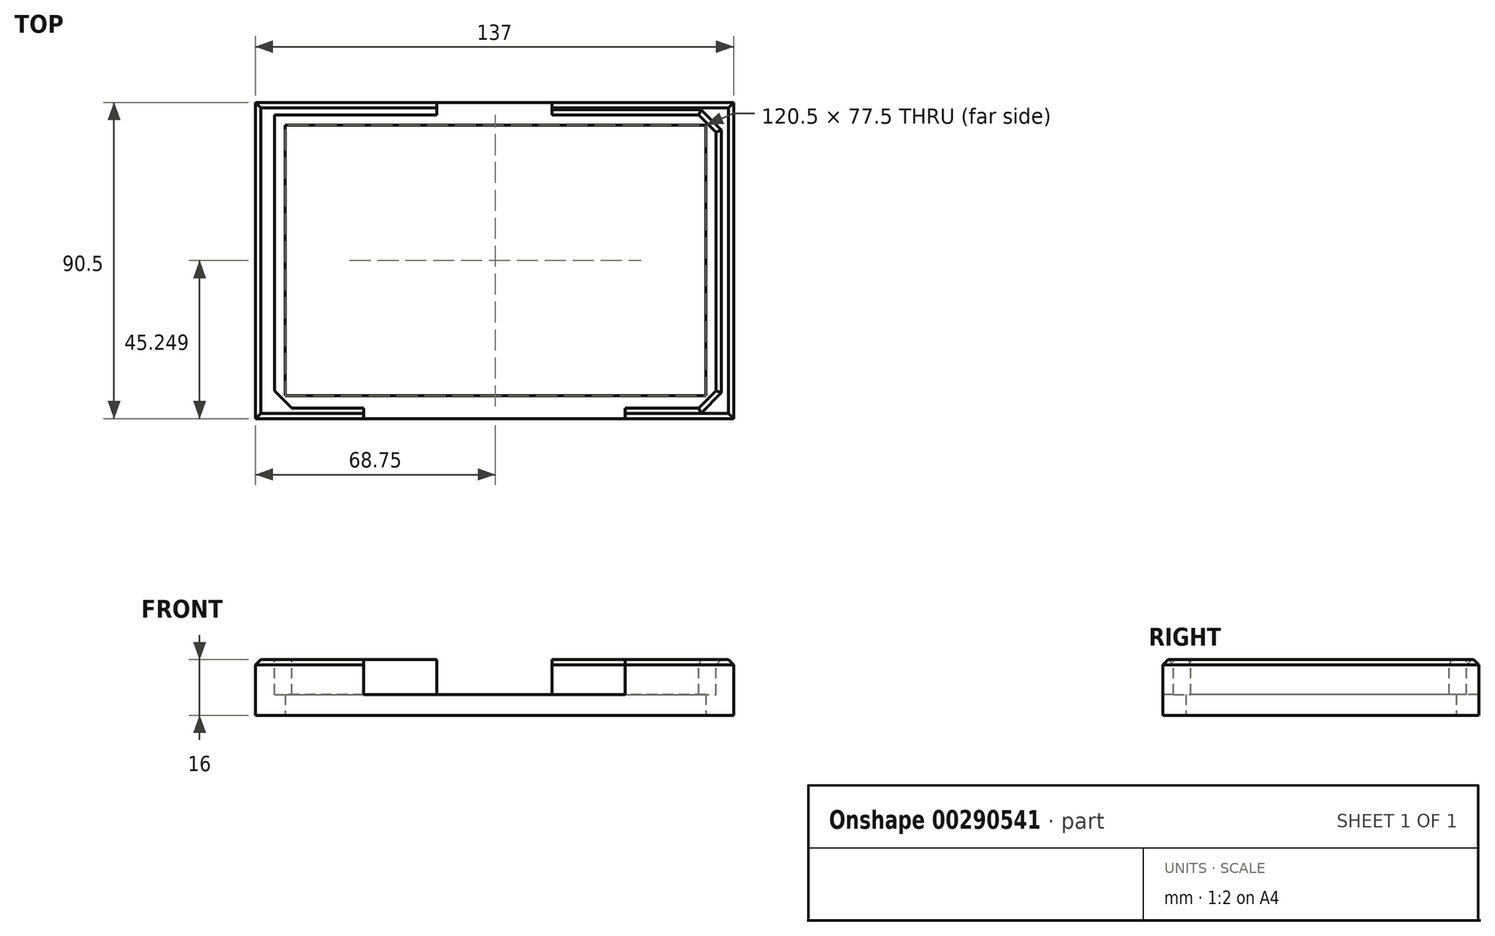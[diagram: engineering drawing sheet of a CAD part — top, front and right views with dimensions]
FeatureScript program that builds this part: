
annotation { "Feature Type Name" : "Feature", "Feature Type Description" : "" }
export const myFeature = defineFeature(function(context is Context, id is Id, definition is map)
    precondition{}
    {
        {
            var Q0;
            Q0=qCreatedBy(makeId("Top.planeOp"),FACE);
            var sketch = newSketch(context, id + "F0", { "sketchPlane" : qUnion([Q0])});
            skLineSegment(sketch, "E0.top", {"start": v(-58.19, -26.41) * mm, "end": v(78.81, -26.41) * mm});
            skLineSegment(sketch, "E0.left", {"start": v(-58.19, 64.09) * mm, "end": v(-58.19, -26.41) * mm});
            skLineSegment(sketch, "E0.right", {"start": v(78.81, 64.09) * mm, "end": v(78.81, -26.41) * mm});
            skLineSegment(sketch, "E1.top", {"start": v(-49.69, -19.91) * mm, "end": v(70.81, -19.91) * mm});
            skLineSegment(sketch, "E1.left", {"start": v(-49.69, 57.59) * mm, "end": v(-49.69, -19.91) * mm});
            skLineSegment(sketch, "E1.right", {"start": v(70.81, 57.59) * mm, "end": v(70.81, -19.91) * mm});
            skLineSegment(sketch, "E2", {"start": v(-58.19, 64.09) * mm, "end": v(78.81, 64.09) * mm});
            skLineSegment(sketch, "E3", {"start": v(70.81, 57.59) * mm, "end": v(-49.69, 57.59) * mm});
            skSolve(sketch);
        }
        {
            var Q0;
            Q0=makeQuery(id+"F0.imprint","IMPRINT",FACE,{"disambiguationData":[TD([[makeQuery(id+"F0.imprint","IMPRINT",EDGE,{"derivedFrom":sQuery(id+"F0.wireOp",EDGE,"E0.top")}),1.0]])]});
            extrude(context, id + "F1", {"entities" : qUnion([Q0]), "depth" : 16 * mm});
        }
        {
            var Q0;
            Q0=makeQuery(id+"F1.opExtrude","CAP_VERTEX",VERTEX,{"disambiguationData":[OSD([sQuery(id+"F0.wireOp",EDGE,"E0.left"),sQuery(id+"F0.wireOp",EDGE,"E2")])],"isStart":false});
            var Q1;
            Q1=makeQuery(id+"F1.opExtrude","CAP_VERTEX",VERTEX,{"disambiguationData":[OSD([sQuery(id+"F0.wireOp",EDGE,"E1.left"),sQuery(id+"F0.wireOp",EDGE,"E3")])],"isStart":false});
            var Q2;
            Q2=makeQuery(id+"F1.opExtrude","CAP_VERTEX",VERTEX,{"disambiguationData":[OSD([sQuery(id+"F0.wireOp",EDGE,"E1.top"),sQuery(id+"F0.wireOp",EDGE,"E1.left")])],"isStart":false});
            cPlane(context, id + "F2", {"entities" : qUnion([Q0, Q1, Q2]), "cplaneType" : CPlaneType.THREE_POINT, "offset" : 25 * mm, "width" : 150 * mm, "height" : 150 * mm});
        }
        {
            var Q0;
            Q0=qCreatedBy(id+"F2.planeOp",FACE);
            var sketch = newSketch(context, id + "F3", { "sketchPlane" : qUnion([Q0])});
            skLineSegment(sketch, "E4.bottom", {"start": v(-6.19, 80.88) * mm, "end": v(26.81, 80.88) * mm});
            skLineSegment(sketch, "E4.top", {"start": v(-6.19, 32.2) * mm, "end": v(26.81, 32.2) * mm});
            skLineSegment(sketch, "E4.left", {"start": v(-6.19, 80.88) * mm, "end": v(-6.19, 32.2) * mm});
            skLineSegment(sketch, "E4.right", {"start": v(26.81, 80.88) * mm, "end": v(26.81, 32.2) * mm});
            skLineSegment(sketch, "E5.bottom", {"start": v(-52.69, 60.59) * mm, "end": v(68.81, 60.59) * mm});
            skLineSegment(sketch, "E5.top", {"start": v(-47.69, -23.41) * mm, "end": v(68.81, -23.41) * mm});
            skLineSegment(sketch, "E5.left", {"start": v(-52.69, 60.59) * mm, "end": v(-52.69, -18.41) * mm});
            skLineSegment(sketch, "E6.bottom", {"start": v(47.81, -13.81) * mm, "end": v(-27.19, -13.81) * mm});
            skLineSegment(sketch, "E6.top", {"start": v(47.81, -33.81) * mm, "end": v(-27.19, -33.81) * mm});
            skLineSegment(sketch, "E6.left", {"start": v(47.81, -13.81) * mm, "end": v(47.81, -33.81) * mm});
            skLineSegment(sketch, "E6.right", {"start": v(-27.19, -13.81) * mm, "end": v(-27.19, -33.81) * mm});
            skLineSegment(sketch, "E7", {"start": v(-52.69, -18.41) * mm, "end": v(-47.69, -23.41) * mm});
            skLineSegment(sketch, "E8", {"start": v(68.81, -23.41) * mm, "end": v(73.81, -18.41) * mm});
            skLineSegment(sketch, "E9", {"start": v(68.81, 60.59) * mm, "end": v(73.81, 55.59) * mm});
            skLineSegment(sketch, "E10", {"start": v(73.81, 55.59) * mm, "end": v(73.81, -18.41) * mm});
            skSolve(sketch);
        }
        {
            var Q0;
            {var subQ0=sQuery(id+"F3.wireOp",EDGE,"E4.bottom");Q0=makeQuery(id+"F3.imprint","IMPRINT",FACE,{"disambiguationData":[TD([[makeQuery(id+"F3.imprint","IMPRINT",EDGE,{"derivedFrom":subQ0}),-1.0]])]});}
            var Q1;
            {var subQ0=sQuery(id+"F3.wireOp",EDGE,"E4.top");Q1=makeQuery(id+"F3.imprint","IMPRINT",FACE,{"disambiguationData":[TD([[makeQuery(id+"F3.imprint","IMPRINT",EDGE,{"derivedFrom":subQ0}),1.0]])]});}
            var Q2;
            {var subQ10=sQuery(id+"F3.wireOp",EDGE,"E4.top");Q2=makeQuery(id+"F3.imprint","IMPRINT",FACE,{"disambiguationData":[TD([[makeQuery(id+"F3.imprint","IMPRINT",EDGE,{"derivedFrom":subQ10}),-1.0]])]});}
            var Q3;
            {var subQ5=sQuery(id+"F3.wireOp",EDGE,"E6.bottom");Q3=makeQuery(id+"F3.imprint","IMPRINT",FACE,{"disambiguationData":[TD([[makeQuery(id+"F3.imprint","IMPRINT",EDGE,{"derivedFrom":subQ5}),1.0]])]});}
            var Q4;
            {var subQ5=sQuery(id+"F3.wireOp",EDGE,"E6.top");Q4=makeQuery(id+"F3.imprint","IMPRINT",FACE,{"disambiguationData":[TD([[makeQuery(id+"F3.imprint","IMPRINT",EDGE,{"derivedFrom":subQ5}),-1.0]])]});}
            extrude(context, id + "F4", {"entities" : qUnion([Q0, Q1, Q2, Q3, Q4]), "operationType" : NewBodyOperationType.REMOVE, "oppositeDirection" : true, "depth" : 10 * mm});
        }
        {
            var Q0;
            Q0=makeQuery(id+"F4.boolean.opBoolean","COPY",EDGE,{"derivedFrom":makeQuery(id+"F4.opExtrude","CAP_EDGE",EDGE,{"disambiguationData":[OSD([sQuery(id+"F3.wireOp",EDGE,"E5.left")])],"isStart":true})});
            var Q1;
            {var subQ0=sQuery(id+"F3.wireOp",EDGE,"E5.bottom");Q1=makeQuery(id+"F4.boolean.opBoolean","COPY",EDGE,{"derivedFrom":makeQuery(id+"F4.opExtrude","CAP_EDGE",EDGE,{"disambiguationData":[OSD([subQ0]),TDD([makeQuery(id+"F3.imprint","IMPRINT",EDGE,{"disambiguationData":[TD([[makeQuery(id+"F3.imprint","INTERSECT",VERTEX,{"derivedFrom":[subQ0,sQuery(id+"F3.wireOp",EDGE,"E5.left")]}),-1.0]])],"derivedFrom":subQ0})])],"isStart":true})});}
            var Q2;
            {var subQ0=sQuery(id+"F3.wireOp",EDGE,"E5.bottom");Q2=makeQuery(id+"F4.boolean.opBoolean","COPY",EDGE,{"derivedFrom":makeQuery(id+"F4.opExtrude","CAP_EDGE",EDGE,{"disambiguationData":[OSD([subQ0]),TDD([makeQuery(id+"F3.imprint","IMPRINT",EDGE,{"disambiguationData":[TD([[makeQuery(id+"F3.imprint","INTERSECT",VERTEX,{"derivedFrom":[subQ0,sQuery(id+"F3.wireOp",EDGE,"E5.right")]}),1.0]])],"derivedFrom":subQ0})])],"isStart":true})});}
            var Q3;
            Q3=makeQuery(id+"F4.boolean.opBoolean","COPY",EDGE,{"derivedFrom":makeQuery(id+"F4.opExtrude","CAP_EDGE",EDGE,{"disambiguationData":[OSD([sQuery(id+"F3.wireOp",EDGE,"E5.right")])],"isStart":true})});
            var Q4;
            {var subQ0=sQuery(id+"F3.wireOp",EDGE,"E5.top");Q4=makeQuery(id+"F4.boolean.opBoolean","COPY",EDGE,{"derivedFrom":makeQuery(id+"F4.opExtrude","CAP_EDGE",EDGE,{"disambiguationData":[OSD([subQ0]),TDD([makeQuery(id+"F3.imprint","IMPRINT",EDGE,{"disambiguationData":[TD([[makeQuery(id+"F3.imprint","INTERSECT",VERTEX,{"derivedFrom":[subQ0,sQuery(id+"F3.wireOp",EDGE,"E5.right")]}),1.0]])],"derivedFrom":subQ0})])],"isStart":true})});}
            var Q5;
            {var subQ0=sQuery(id+"F3.wireOp",EDGE,"E5.top");Q5=makeQuery(id+"F4.boolean.opBoolean","COPY",EDGE,{"derivedFrom":makeQuery(id+"F4.opExtrude","CAP_EDGE",EDGE,{"disambiguationData":[OSD([subQ0]),TDD([makeQuery(id+"F3.imprint","IMPRINT",EDGE,{"disambiguationData":[TD([[makeQuery(id+"F3.imprint","INTERSECT",VERTEX,{"derivedFrom":[subQ0,sQuery(id+"F3.wireOp",EDGE,"E5.left")]}),-1.0]])],"derivedFrom":subQ0})])],"isStart":true})});}
            var Q6;
            Q6=makeQuery(id+"F1.opExtrude","CAP_EDGE",EDGE,{"disambiguationData":[OSD([sQuery(id+"F0.wireOp",EDGE,"E0.right")])],"isStart":false});
            var Q7;
            {var subQ0=sQuery(id+"F0.wireOp",EDGE,"E0.top");var subQ1=sQuery(id+"F0.wireOp",EDGE,"E0.right");Q7=makeQuery(id+"F4.boolean.opBoolean","SPLIT",EDGE,{"disambiguationData":[TD([makeQuery(id+"F1.opExtrude","SWEPT_FACE",FACE,{"disambiguationData":[OSD([subQ1])]})])],"derivedFrom":makeQuery(id+"F1.opExtrude","CAP_EDGE",EDGE,{"disambiguationData":[OSD([subQ0])],"isStart":false})});}
            var Q8;
            {var subQ0=sQuery(id+"F0.wireOp",EDGE,"E2");var subQ1=sQuery(id+"F0.wireOp",EDGE,"E0.right");Q8=makeQuery(id+"F4.boolean.opBoolean","SPLIT",EDGE,{"disambiguationData":[TD([makeQuery(id+"F1.opExtrude","SWEPT_FACE",FACE,{"disambiguationData":[OSD([subQ1])]})])],"derivedFrom":makeQuery(id+"F1.opExtrude","CAP_EDGE",EDGE,{"disambiguationData":[OSD([subQ0])],"isStart":false})});}
            var Q9;
            {var subQ0=sQuery(id+"F0.wireOp",EDGE,"E2");var subQ1=sQuery(id+"F0.wireOp",EDGE,"E0.left");Q9=makeQuery(id+"F4.boolean.opBoolean","SPLIT",EDGE,{"disambiguationData":[TD([makeQuery(id+"F1.opExtrude","SWEPT_FACE",FACE,{"disambiguationData":[OSD([subQ1])]})])],"derivedFrom":makeQuery(id+"F1.opExtrude","CAP_EDGE",EDGE,{"disambiguationData":[OSD([subQ0])],"isStart":false})});}
            var Q10;
            Q10=makeQuery(id+"F1.opExtrude","CAP_EDGE",EDGE,{"disambiguationData":[OSD([sQuery(id+"F0.wireOp",EDGE,"E0.left")])],"isStart":false});
            var Q11;
            {var subQ0=sQuery(id+"F0.wireOp",EDGE,"E0.top");var subQ1=sQuery(id+"F0.wireOp",EDGE,"E0.left");Q11=makeQuery(id+"F4.boolean.opBoolean","SPLIT",EDGE,{"disambiguationData":[TD([makeQuery(id+"F1.opExtrude","SWEPT_FACE",FACE,{"disambiguationData":[OSD([subQ1])]})])],"derivedFrom":makeQuery(id+"F1.opExtrude","CAP_EDGE",EDGE,{"disambiguationData":[OSD([subQ0])],"isStart":false})});}
            var Q12;
            Q12=makeQuery(id+"F4.boolean.opBoolean","COPY",EDGE,{"derivedFrom":makeQuery(id+"F4.opExtrude","CAP_EDGE",EDGE,{"disambiguationData":[OSD([sQuery(id+"F3.wireOp",EDGE,"E9")])],"isStart":true})});
            var Q13;
            Q13=makeQuery(id+"F4.boolean.opBoolean","COPY",EDGE,{"derivedFrom":makeQuery(id+"F4.opExtrude","CAP_EDGE",EDGE,{"disambiguationData":[OSD([sQuery(id+"F3.wireOp",EDGE,"E10")])],"isStart":true})});
            var Q14;
            Q14=makeQuery(id+"F4.boolean.opBoolean","COPY",EDGE,{"derivedFrom":makeQuery(id+"F4.opExtrude","CAP_EDGE",EDGE,{"disambiguationData":[OSD([sQuery(id+"F3.wireOp",EDGE,"E8")])],"isStart":true})});
            var Q15;
            Q15=makeQuery(id+"F4.boolean.opBoolean","COPY",EDGE,{"derivedFrom":makeQuery(id+"F4.opExtrude","CAP_EDGE",EDGE,{"disambiguationData":[OSD([sQuery(id+"F3.wireOp",EDGE,"E7")])],"isStart":true})});
            chamfer(context, id + "F5", {"entities" : qUnion([Q0, Q1, Q2, Q3, Q4, Q5, Q6, Q7, Q8, Q9, Q10, Q11, Q12, Q13, Q14, Q15]), "width" : 1.5 * mm, "tangentPropagation" : true});
        }
    });
